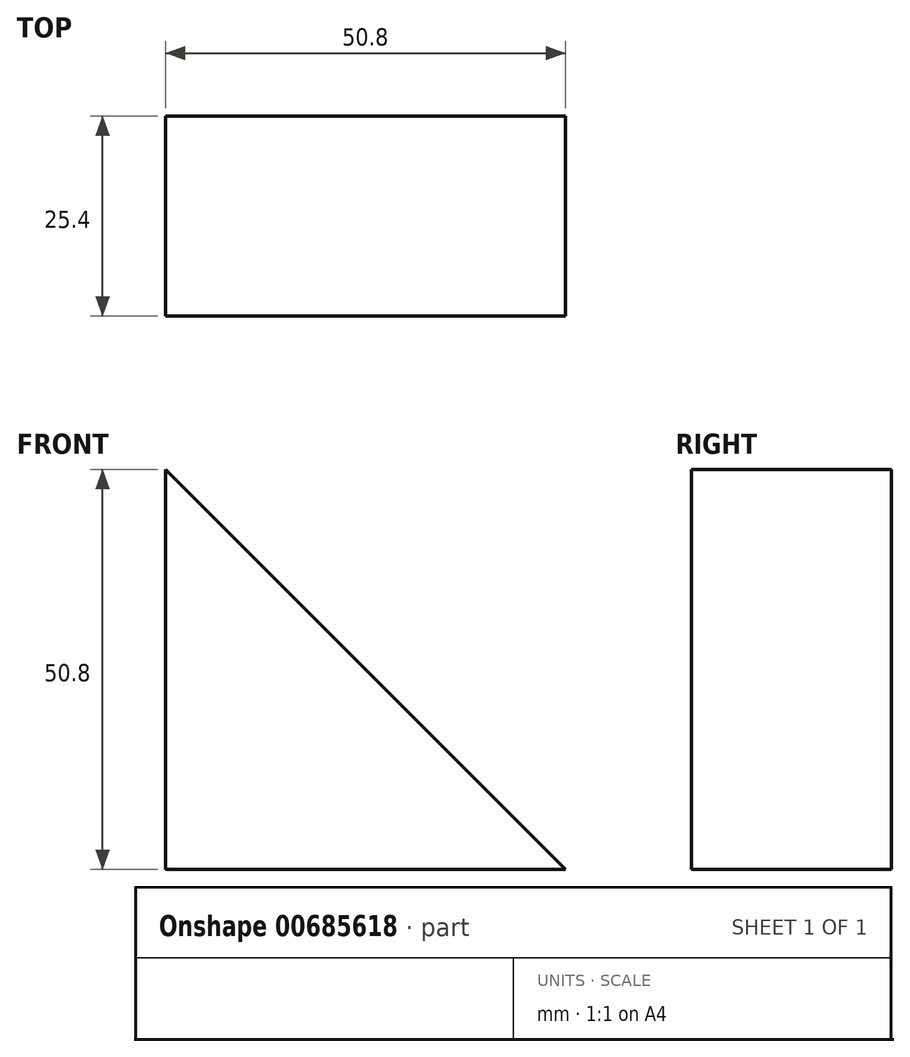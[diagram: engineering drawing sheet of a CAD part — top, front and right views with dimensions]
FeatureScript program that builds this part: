
annotation { "Feature Type Name" : "Feature", "Feature Type Description" : "" }
export const myFeature = defineFeature(function(context is Context, id is Id, definition is map)
    precondition{}
    {
        {
            var Q0;
            Q0=qCreatedBy(makeId("Front.planeOp"),FACE);
            var sketch = newSketch(context, id + "F0", { "sketchPlane" : qUnion([Q0])});
            skLineSegment(sketch, "E0", {"start": v(-62.9, 0) * mm, "end": v(-62.9, 50.8) * mm});
            skLineSegment(sketch, "E1", {"start": v(-62.9, 0) * mm, "end": v(-12.1, 0) * mm});
            skLineSegment(sketch, "E2", {"start": v(-62.9, 50.8) * mm, "end": v(-12.1, 0) * mm});
            skSolve(sketch);
        }
        {
            var Q0;
            Q0 = qSketchRegion(id + "F0", true);
            extrude(context, id + "F1", {"entities" : qUnion([Q0]), "depth" : 25.4 * mm, "offsetDistance" : 25.4 * mm});
        }
    });
